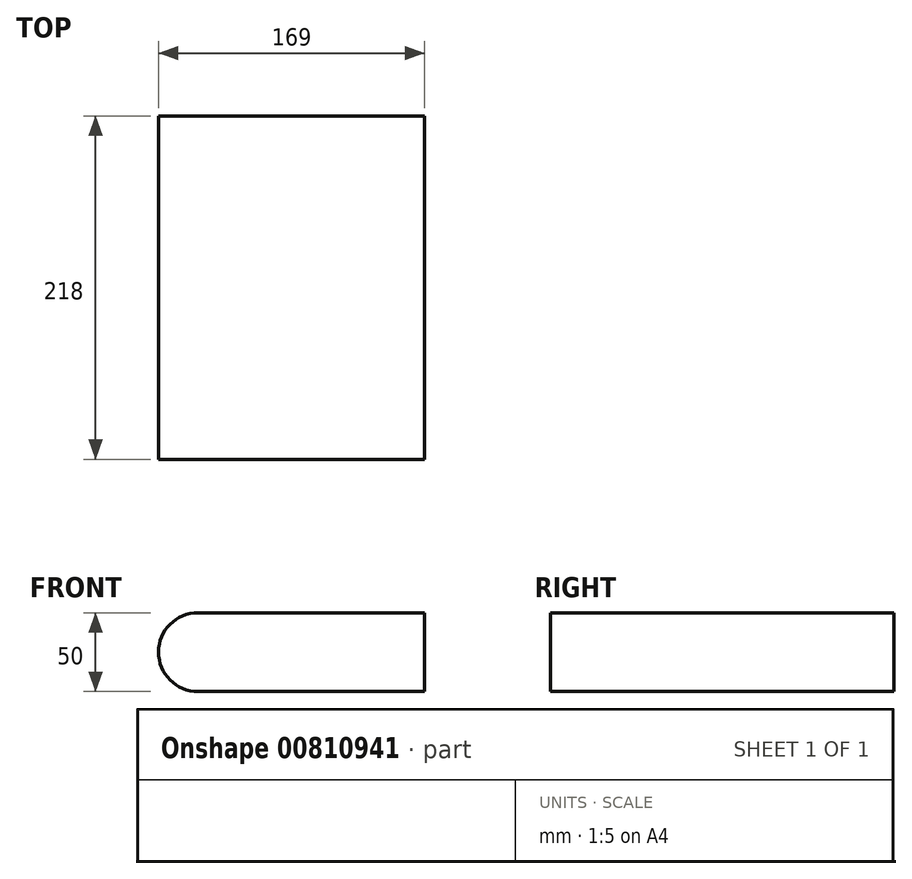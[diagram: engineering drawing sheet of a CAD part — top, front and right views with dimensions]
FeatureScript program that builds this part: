
annotation { "Feature Type Name" : "Feature", "Feature Type Description" : "" }
export const myFeature = defineFeature(function(context is Context, id is Id, definition is map)
    precondition{}
    {
        {
            var Q0;
            Q0=qCreatedBy(makeId("Front.planeOp"),FACE);
            var sketch = newSketch(context, id + "F0", { "sketchPlane" : qUnion([Q0])});
            skLineSegment(sketch, "E0", {"start": v(-54.42, 22.5) * mm, "end": v(89.58, 22.5) * mm});
            skLineSegment(sketch, "E1", {"start": v(89.58, 22.5) * mm, "end": v(89.58, -27.5) * mm});
            skLineSegment(sketch, "E2", {"start": v(89.58, -27.5) * mm, "end": v(-54.42, -27.5) * mm});
            skArc(sketch, "E3", {"start": v(-54.42, 22.5) * mm, "mid": v(-79.42, -2.5) * mm, "end": v(-54.42, -27.5) * mm});
            skSolve(sketch);
        }
        {
            var Q0;
            Q0 = qSketchRegion(id + "F0", true);
            extrude(context, id + "F1", {"entities" : qUnion([Q0]), "endBound" : BoundingType.SYMMETRIC, "depth" : 218 * mm, "offsetDistance" : 25 * mm});
        }
    });
